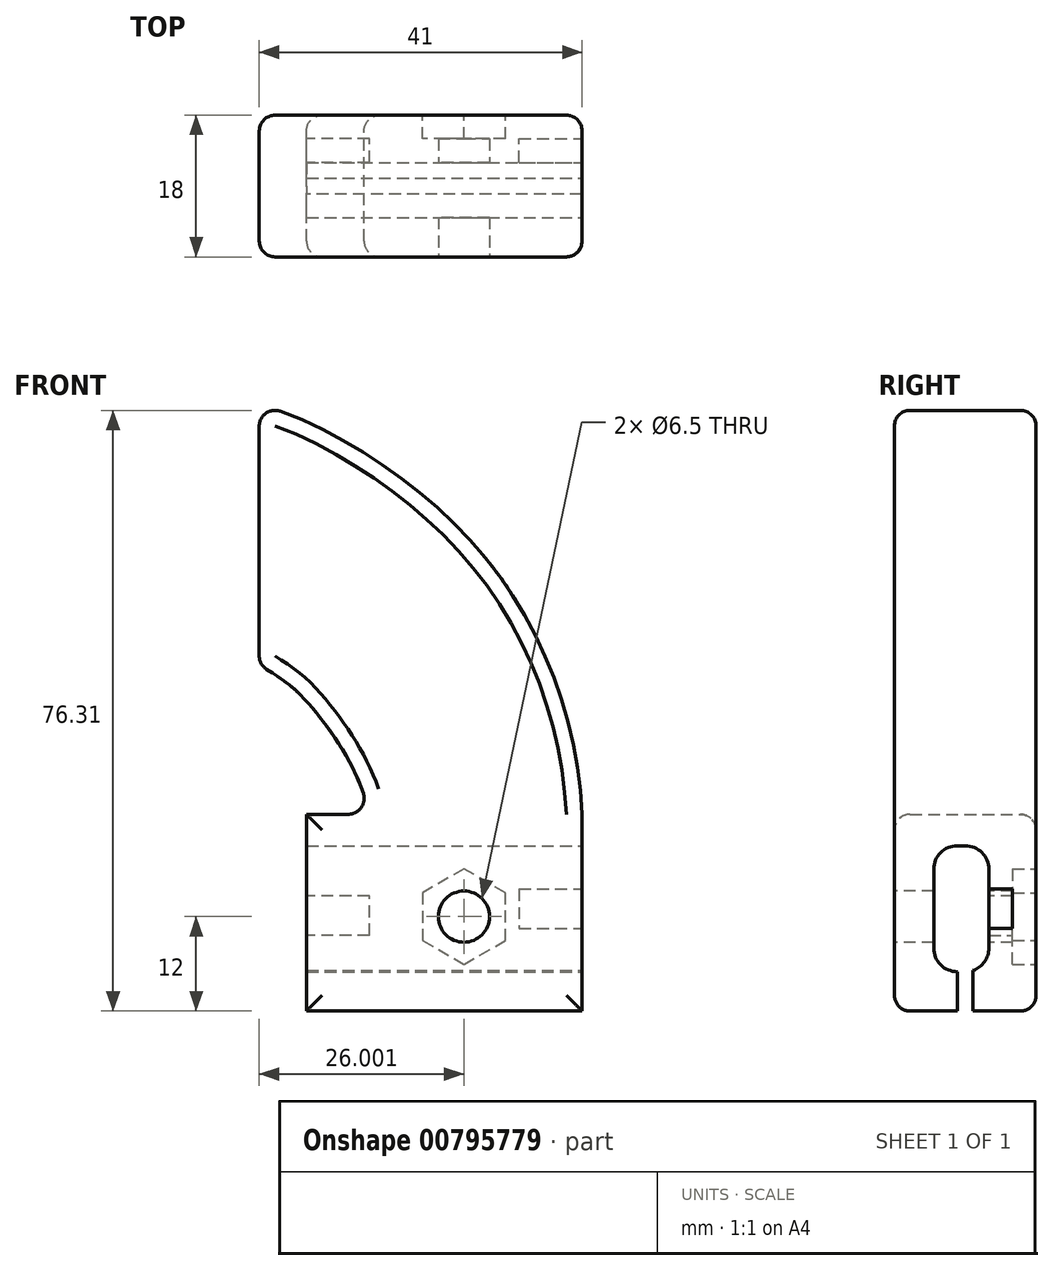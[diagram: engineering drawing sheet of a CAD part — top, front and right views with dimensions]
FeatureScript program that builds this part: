
annotation { "Feature Type Name" : "Feature", "Feature Type Description" : "" }
export const myFeature = defineFeature(function(context is Context, id is Id, definition is map)
    precondition{}
    {
        {
            var Q0;
            Q0=qCreatedBy(makeId("Front.planeOp"),FACE);
            var sketch = newSketch(context, id + "F0", { "sketchPlane" : qUnion([Q0])});
            skLineSegment(sketch, "E0", {"start": v(-16.15, -30.33) * mm, "end": v(18.85, -30.33) * mm});
            skLineSegment(sketch, "E1", {"start": v(18.85, -30.33) * mm, "end": v(18.85, -5.33) * mm});
            skLineSegment(sketch, "E2", {"start": v(-16.15, -30.33) * mm, "end": v(-16.15, -5.33) * mm});
            skLineSegment(sketch, "E3", {"start": v(-16.15, -5.33) * mm, "end": v(-8.3, -5.33) * mm});
            skFitSpline(sketch, "E4", {"points": [v(-8.3, -5.33) * mm, v(-15.26, 8.02) * mm, v(-22.15, 13.67) * mm], "startDerivative": vector(-3.64, 25.66) * mm, "endDerivative": vector(-23.88, 14.5) * mm});
            skLineSegment(sketch, "E5", {"start": v(-22.15, 13.67) * mm, "end": v(-22.15, 46.67) * mm});
            skFitSpline(sketch, "E6", {"points": [v(-22.15, 46.67) * mm, v(-1.25, 35.1) * mm, v(12.26, 18.65) * mm, v(18.85, -5.33) * mm], "startDerivative": vector(59.19, -14.76) * mm, "endDerivative": vector(3.88, -80.48) * mm});
            skSolve(sketch);
        }
        {
            var Q0;
            Q0=makeQuery(id+"F0.imprint","IMPRINT",FACE,{"disambiguationData":[TD([[makeQuery(id+"F0.imprint","IMPRINT",EDGE,{"derivedFrom":sQuery(id+"F0.wireOp",EDGE,"E0")}),1.0]])]});
            extrude(context, id + "F1", {"entities" : qUnion([Q0]), "depth" : 18 * mm, "offsetDistance" : 25 * mm});
        }
        {
            var Q0;
            Q0=makeQuery(id+"F1.opExtrude","SWEPT_FACE",FACE,{"disambiguationData":[OSD([sQuery(id+"F0.wireOp",EDGE,"E1")])]});
            var sketch = newSketch(context, id + "F2", { "sketchPlane" : qUnion([Q0])});
            skLineSegment(sketch, "E7.bottom", {"start": v(-13, -9.33) * mm, "end": v(-6, -9.33) * mm});
            skLineSegment(sketch, "E7.top", {"start": v(-13, -25.33) * mm, "end": v(-6, -25.33) * mm});
            skLineSegment(sketch, "E7.left", {"start": v(-13, -9.33) * mm, "end": v(-13, -25.33) * mm});
            skLineSegment(sketch, "E7.right", {"start": v(-6, -9.33) * mm, "end": v(-6, -25.33) * mm});
            skLineSegment(sketch, "E8", {"start": v(-6, -14.83) * mm, "end": v(-3, -14.83) * mm});
            skLineSegment(sketch, "E9", {"start": v(-3, -14.83) * mm, "end": v(-3, -19.83) * mm});
            skLineSegment(sketch, "E10", {"start": v(-3, -19.83) * mm, "end": v(-6, -19.83) * mm});
            skPoint(sketch, "E11", {"position": v(-4.5, -17.33) * mm});
            skPoint(sketch, "E11.positionSnap0", {"position": v(-3, -17.33) * mm});
            skPoint(sketch, "E11.positionSnap1", {"position": v(-4.5, -14.83) * mm});
            skSolve(sketch);
        }
        {
            var Q0;
            Q0=makeQuery(id+"F2.imprint","IMPRINT",FACE,{"disambiguationData":[TD([[makeQuery(id+"F2.imprint","IMPRINT",EDGE,{"derivedFrom":sQuery(id+"F2.wireOp",EDGE,"E7.bottom")}),-1.0]])]});
            extrude(context, id + "F3", {"entities" : qUnion([Q0]), "operationType" : NewBodyOperationType.REMOVE, "oppositeDirection" : true, "depth" : 36.3 * mm, "offsetDistance" : 25 * mm});
        }
        {
            var Q0;
            Q0=makeQuery(id+"F3.boolean.opBoolean","COPY",EDGE,{"derivedFrom":makeQuery(id+"F3.opExtrude","SWEPT_EDGE",EDGE,{"disambiguationData":[OSD([sQuery(id+"F2.wireOp",EDGE,"E7.bottom"),sQuery(id+"F2.wireOp",EDGE,"E7.left")])]})});
            var Q1;
            Q1=makeQuery(id+"F3.boolean.opBoolean","COPY",EDGE,{"derivedFrom":makeQuery(id+"F3.opExtrude","SWEPT_EDGE",EDGE,{"disambiguationData":[OSD([sQuery(id+"F2.wireOp",EDGE,"E7.bottom"),sQuery(id+"F2.wireOp",EDGE,"E7.right")])]})});
            var Q2;
            Q2=makeQuery(id+"F3.boolean.opBoolean","COPY",EDGE,{"derivedFrom":makeQuery(id+"F3.opExtrude","SWEPT_EDGE",EDGE,{"disambiguationData":[OSD([sQuery(id+"F2.wireOp",EDGE,"E7.top"),sQuery(id+"F2.wireOp",EDGE,"E7.left")])]})});
            var Q3;
            Q3=makeQuery(id+"F3.boolean.opBoolean","COPY",EDGE,{"derivedFrom":makeQuery(id+"F3.opExtrude","SWEPT_EDGE",EDGE,{"disambiguationData":[OSD([sQuery(id+"F2.wireOp",EDGE,"E7.top"),sQuery(id+"F2.wireOp",EDGE,"E7.right")])]})});
            fillet(context, id + "F4", {"entities" : qUnion([Q0, Q1, Q2, Q3]), "radius" : 3 * mm, "tangentPropagation" : true, "allowEdgeOverflow" : false});
        }
        {
            var Q0;
            {var subQ0=sQuery(id+"F2.wireOp",EDGE,"E8");Q0=makeQuery(id+"F2.imprint","IMPRINT",FACE,{"disambiguationData":[TD([[makeQuery(id+"F2.imprint","IMPRINT",EDGE,{"derivedFrom":subQ0}),-1.0]])]});}
            extrude(context, id + "F5", {"entities" : qUnion([Q0]), "operationType" : NewBodyOperationType.REMOVE, "oppositeDirection" : true, "depth" : 8 * mm, "offsetDistance" : 25 * mm});
        }
        {
            var Q0;
            Q0=makeQuery(id+"F1.opExtrude","CAP_FACE",FACE,{"disambiguationData":[OSD([sQuery(id+"F0.wireOp",EDGE,"E0"),sQuery(id+"F0.wireOp",EDGE,"E1"),sQuery(id+"F0.wireOp",EDGE,"E2"),sQuery(id+"F0.wireOp",EDGE,"E3"),sQuery(id+"F0.wireOp",EDGE,"E4"),sQuery(id+"F0.wireOp",EDGE,"E5"),sQuery(id+"F0.wireOp",EDGE,"E6")])],"isStart":false});
            var sketch = newSketch(context, id + "F6", { "sketchPlane" : qUnion([Q0])});
            skPoint(sketch, "E12", {"position": v(3.85, -18.33) * mm});
            skSolve(sketch);
        }
        {
            var Q0;
            Q0=sQuery(id+"F6.wireOp",VERTEX,"E12");
            var Q1;
            Q1=makeQuery(id+"F1.opExtrude","SWEPT_BODY",BODY,{"disambiguationData":[OSD([sQuery(id+"F0.wireOp",EDGE,"E0"),sQuery(id+"F0.wireOp",EDGE,"E1"),sQuery(id+"F0.wireOp",EDGE,"E2"),sQuery(id+"F0.wireOp",EDGE,"E3"),sQuery(id+"F0.wireOp",EDGE,"E4"),sQuery(id+"F0.wireOp",EDGE,"E5"),sQuery(id+"F0.wireOp",EDGE,"E6")])]});
            hole(context, id + "F7", {"style" : HoleStyle.SIMPLE, "endStyle" : HoleEndStyle.THROUGH, "holeDiameter" : 6.5 * mm, "majorDiameter" : 5 * mm, "isTappedThrough" : true, "tappedDepth" : 12 * mm, "tapClearance" : 3, "locations" : qUnion([Q0]), "scope" : qUnion([Q1])});
        }
        {
            var Q0;
            Q0=makeQuery(id+"F1.opExtrude","SWEPT_FACE",FACE,{"disambiguationData":[OSD([sQuery(id+"F0.wireOp",EDGE,"E2")])]});
            var sketch = newSketch(context, id + "F8", { "sketchPlane" : qUnion([Q0])});
            skLineSegment(sketch, "E13", {"start": v(6, -15.7) * mm, "end": v(6, -20.7) * mm});
            skLineSegment(sketch, "E14", {"start": v(6, -20.7) * mm, "end": v(3, -20.7) * mm});
            skLineSegment(sketch, "E15", {"start": v(3, -20.7) * mm, "end": v(3, -15.7) * mm});
            skLineSegment(sketch, "E16", {"start": v(3, -15.7) * mm, "end": v(6, -15.7) * mm});
            skLineSegment(sketch, "E17", {"start": v(6, -20.7) * mm, "end": v(6, -15.7) * mm});
            skPoint(sketch, "E18.positionSnap0", {"position": v(6, -17.33) * mm});
            skPoint(sketch, "E18.positionSnap1", {"position": v(4.5, -15.7) * mm});
            skPoint(sketch, "E19", {"position": v(4.5, -18.2) * mm});
            skPoint(sketch, "E19.positionSnap0", {"position": v(3, -18.2) * mm});
            skSolve(sketch);
        }
        {
            var Q0;
            Q0=makeQuery(id+"F8.imprint","IMPRINT",FACE,{"disambiguationData":[TD([[makeQuery(id+"F8.imprint","IMPRINT",EDGE,{"derivedFrom":sQuery(id+"F8.wireOp",EDGE,"E14")}),-1.0]])]});
            extrude(context, id + "F9", {"entities" : qUnion([Q0]), "operationType" : NewBodyOperationType.REMOVE, "oppositeDirection" : true, "depth" : 8 * mm, "offsetDistance" : 25 * mm});
        }
        {
            var Q0;
            Q0=makeQuery(id+"F1.opExtrude","CAP_FACE",FACE,{"disambiguationData":[OSD([sQuery(id+"F0.wireOp",EDGE,"E0"),sQuery(id+"F0.wireOp",EDGE,"E1"),sQuery(id+"F0.wireOp",EDGE,"E2"),sQuery(id+"F0.wireOp",EDGE,"E3"),sQuery(id+"F0.wireOp",EDGE,"E4"),sQuery(id+"F0.wireOp",EDGE,"E5"),sQuery(id+"F0.wireOp",EDGE,"E6")])],"isStart":true});
            var sketch = newSketch(context, id + "F10", { "sketchPlane" : qUnion([Q0])});
            skPoint(sketch, "E20", {"position": v(-3.85, -18.33) * mm});
            skCircle(sketch, "E21.cCircle", {"center": v(-3.85, -18.33) * mm, "radius": 5.25 * mm, "construction": true});
            skLineSegment(sketch, "E21.0", {"start": v(-3.85, -12.27) * mm, "end": v(1.4, -15.3) * mm});
            skLineSegment(sketch, "E21.1", {"start": v(1.4, -15.3) * mm, "end": v(1.4, -21.36) * mm});
            skLineSegment(sketch, "E21.2", {"start": v(1.4, -21.36) * mm, "end": v(-3.85, -24.4) * mm});
            skLineSegment(sketch, "E21.3", {"start": v(-3.85, -24.4) * mm, "end": v(-9.1, -21.36) * mm});
            skLineSegment(sketch, "E21.4", {"start": v(-9.1, -21.36) * mm, "end": v(-9.1, -15.3) * mm});
            skLineSegment(sketch, "E21.5", {"start": v(-9.1, -15.3) * mm, "end": v(-3.85, -12.27) * mm});
            skPoint(sketch, "E21.0.midPoint", {"position": v(-1.23, -13.78) * mm});
            skSolve(sketch);
        }
        {
            var Q0;
            Q0=makeQuery(id+"F10.imprint","IMPRINT",FACE,{"disambiguationData":[TD([[makeQuery(id+"F10.imprint","IMPRINT",EDGE,{"derivedFrom":sQuery(id+"F10.wireOp",EDGE,"E21.0")}),-1.0]])]});
            extrude(context, id + "F11", {"entities" : qUnion([Q0]), "operationType" : NewBodyOperationType.REMOVE, "oppositeDirection" : true, "depth" : 3 * mm, "offsetDistance" : 25 * mm});
        }
        {
            var Q0;
            Q0=makeQuery(id+"F1.opExtrude","SWEPT_FACE",FACE,{"disambiguationData":[OSD([sQuery(id+"F0.wireOp",EDGE,"E0")])]});
            var sketch = newSketch(context, id + "F12", { "sketchPlane" : qUnion([Q0])});
            skLineSegment(sketch, "E22.bottom", {"start": v(18.85, 10) * mm, "end": v(-16.21, 10) * mm});
            skLineSegment(sketch, "E22.top", {"start": v(18.85, 8) * mm, "end": v(-16.21, 8) * mm});
            skLineSegment(sketch, "E22.left", {"start": v(18.85, 10) * mm, "end": v(18.85, 8) * mm});
            skLineSegment(sketch, "E22.right", {"start": v(-16.21, 10) * mm, "end": v(-16.21, 8) * mm});
            skPoint(sketch, "E23", {"position": v(1.32, 9) * mm});
            skPoint(sketch, "E23.positionSnap0", {"position": v(-16.21, 9) * mm});
            skPoint(sketch, "E23.positionSnap1", {"position": v(1.32, 8) * mm});
            skSolve(sketch);
        }
        {
            var Q0;
            Q0=makeQuery(id+"F12.imprint","IMPRINT",FACE,{"disambiguationData":[TD([[makeQuery(id+"F12.imprint","IMPRINT",EDGE,{"derivedFrom":sQuery(id+"F12.wireOp",EDGE,"E22.bottom")}),1.0]])]});
            extrude(context, id + "F13", {"entities" : qUnion([Q0]), "operationType" : NewBodyOperationType.REMOVE, "oppositeDirection" : true, "depth" : 9.6 * mm, "offsetDistance" : 25 * mm});
        }
        {
            var Q0;
            Q0=makeQuery(id+"F1.opExtrude","CAP_EDGE",EDGE,{"disambiguationData":[OSD([sQuery(id+"F0.wireOp",EDGE,"E2")])],"isStart":false});
            var Q1;
            Q1=makeQuery(id+"F1.opExtrude","CAP_EDGE",EDGE,{"disambiguationData":[OSD([sQuery(id+"F0.wireOp",EDGE,"E0")])],"isStart":false});
            var Q2;
            Q2=makeQuery(id+"F1.opExtrude","CAP_EDGE",EDGE,{"disambiguationData":[OSD([sQuery(id+"F0.wireOp",EDGE,"E6")])],"isStart":false});
            var Q3;
            Q3=makeQuery(id+"F1.opExtrude","CAP_EDGE",EDGE,{"disambiguationData":[OSD([sQuery(id+"F0.wireOp",EDGE,"E1")])],"isStart":false});
            var Q4;
            Q4=makeQuery(id+"F1.opExtrude","CAP_EDGE",EDGE,{"disambiguationData":[OSD([sQuery(id+"F0.wireOp",EDGE,"E4")])],"isStart":false});
            var Q5;
            Q5=makeQuery(id+"F1.opExtrude","CAP_EDGE",EDGE,{"disambiguationData":[OSD([sQuery(id+"F0.wireOp",EDGE,"E5")])],"isStart":false});
            var Q6;
            Q6=makeQuery(id+"F1.opExtrude","CAP_EDGE",EDGE,{"disambiguationData":[OSD([sQuery(id+"F0.wireOp",EDGE,"E5")])],"isStart":true});
            var Q7;
            Q7=makeQuery(id+"F1.opExtrude","CAP_EDGE",EDGE,{"disambiguationData":[OSD([sQuery(id+"F0.wireOp",EDGE,"E6")])],"isStart":true});
            var Q8;
            Q8=makeQuery(id+"F1.opExtrude","CAP_EDGE",EDGE,{"disambiguationData":[OSD([sQuery(id+"F0.wireOp",EDGE,"E1")])],"isStart":true});
            var Q9;
            Q9=makeQuery(id+"F1.opExtrude","CAP_EDGE",EDGE,{"disambiguationData":[OSD([sQuery(id+"F0.wireOp",EDGE,"E0")])],"isStart":true});
            var Q10;
            Q10=makeQuery(id+"F1.opExtrude","CAP_EDGE",EDGE,{"disambiguationData":[OSD([sQuery(id+"F0.wireOp",EDGE,"E2")])],"isStart":true});
            var Q11;
            Q11=makeQuery(id+"F1.opExtrude","CAP_EDGE",EDGE,{"disambiguationData":[OSD([sQuery(id+"F0.wireOp",EDGE,"E4")])],"isStart":true});
            var Q12;
            Q12=makeQuery(id+"F1.opExtrude","CAP_EDGE",EDGE,{"disambiguationData":[OSD([sQuery(id+"F0.wireOp",EDGE,"E3")])],"isStart":true});
            var Q13;
            Q13=makeQuery(id+"F1.opExtrude","CAP_EDGE",EDGE,{"disambiguationData":[OSD([sQuery(id+"F0.wireOp",EDGE,"E3")])],"isStart":false});
            var Q14;
            Q14=makeQuery(id+"F1.opExtrude","SWEPT_EDGE",EDGE,{"disambiguationData":[OSD([sQuery(id+"F0.wireOp",EDGE,"E3"),sQuery(id+"F0.wireOp",EDGE,"E4")])]});
            var Q15;
            Q15=makeQuery(id+"F1.opExtrude","SWEPT_EDGE",EDGE,{"disambiguationData":[OSD([sQuery(id+"F0.wireOp",EDGE,"E4"),sQuery(id+"F0.wireOp",EDGE,"E5")])]});
            var Q16;
            Q16=makeQuery(id+"F1.opExtrude","SWEPT_EDGE",EDGE,{"disambiguationData":[OSD([sQuery(id+"F0.wireOp",EDGE,"E5"),sQuery(id+"F0.wireOp",EDGE,"E6")])]});
            var Q17;
            Q17=makeQuery(id+"F1.opExtrude","SWEPT_EDGE",EDGE,{"disambiguationData":[OSD([sQuery(id+"F0.wireOp",EDGE,"E1"),sQuery(id+"F0.wireOp",EDGE,"E6")])]});
            fillet(context, id + "F14", {"entities" : qUnion([Q0, Q1, Q2, Q3, Q4, Q5, Q6, Q7, Q8, Q9, Q10, Q11, Q12, Q13, Q14, Q15, Q16, Q17]), "radius" : 2 * mm, "tangentPropagation" : true, "allowEdgeOverflow" : false});
        }
    });
